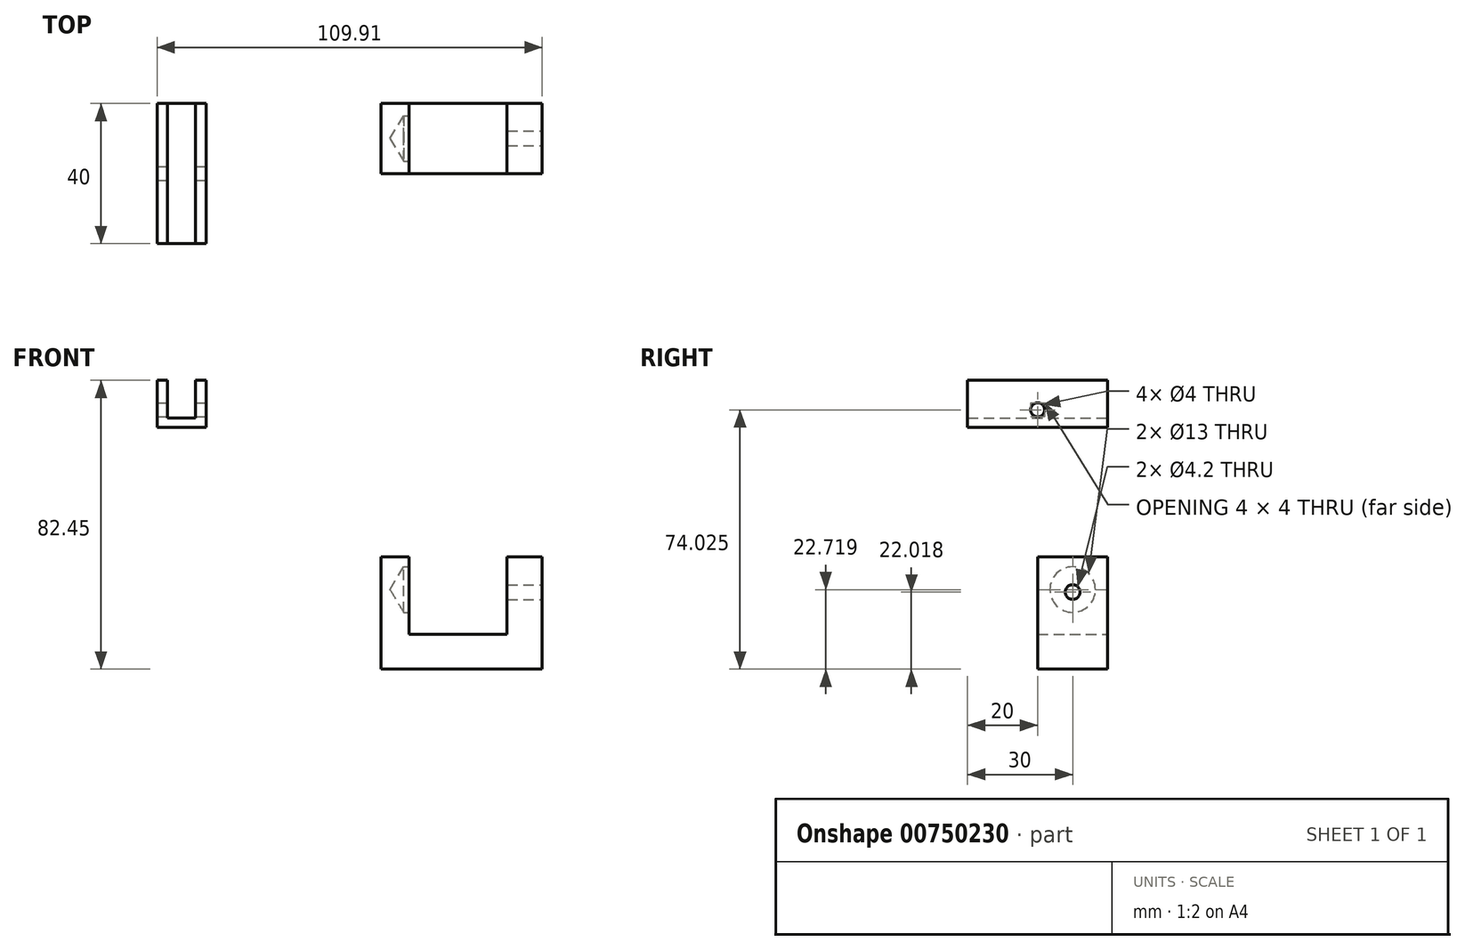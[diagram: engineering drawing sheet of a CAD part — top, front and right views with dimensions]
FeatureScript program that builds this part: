
annotation { "Feature Type Name" : "Feature", "Feature Type Description" : "" }
export const myFeature = defineFeature(function(context is Context, id is Id, definition is map)
    precondition{}
    {
        {
            var Q0;
            Q0=qCreatedBy(makeId("Front.planeOp"),FACE);
            var sketch = newSketch(context, id + "F0", { "sketchPlane" : qUnion([Q0])});
            skLineSegment(sketch, "E0", {"start": v(0, 0) * mm, "end": v(0, -32) * mm});
            skLineSegment(sketch, "E1", {"start": v(0, -32) * mm, "end": v(46, -32) * mm});
            skLineSegment(sketch, "E2", {"start": v(46, -32) * mm, "end": v(46, 0) * mm});
            skLineSegment(sketch, "E3", {"start": v(46, 0) * mm, "end": v(36, 0) * mm});
            skLineSegment(sketch, "E4", {"start": v(36, 0) * mm, "end": v(36, -22) * mm});
            skLineSegment(sketch, "E5", {"start": v(36, -22) * mm, "end": v(8, -22) * mm});
            skLineSegment(sketch, "E6", {"start": v(8, -22) * mm, "end": v(8, 0) * mm});
            skLineSegment(sketch, "E7", {"start": v(8, 0) * mm, "end": v(0, 0) * mm});
            skSolve(sketch);
        }
        {
            var Q0;
            Q0=makeQuery(id+"F0.imprint","IMPRINT",FACE,{"disambiguationData":[TD([[makeQuery(id+"F0.imprint","IMPRINT",EDGE,{"derivedFrom":sQuery(id+"F0.wireOp",EDGE,"E0")}),1.0]])]});
            extrude(context, id + "F1", {"entities" : qUnion([Q0]), "depth" : 20 * mm, "offsetDistance" : 25 * mm});
        }
        {
            var Q0;
            Q0=makeQuery(id+"F1.opExtrude","SWEPT_FACE",FACE,{"disambiguationData":[OSD([sQuery(id+"F0.wireOp",EDGE,"E6")])]});
            var sketch = newSketch(context, id + "F2", { "sketchPlane" : qUnion([Q0])});
            skPoint(sketch, "E8", {"position": v(-10, -9.28) * mm});
            skPoint(sketch, "E8.positionSnap0", {"position": v(-10, 0) * mm});
            skSolve(sketch);
        }
        {
            var Q0;
            Q0=sQuery(id+"F2.wireOp",VERTEX,"E8");
            var Q1;
            Q1=makeQuery(id+"F1.opExtrude","SWEPT_BODY",BODY,{"disambiguationData":[OSD([sQuery(id+"F0.wireOp",EDGE,"E0"),sQuery(id+"F0.wireOp",EDGE,"E1"),sQuery(id+"F0.wireOp",EDGE,"E2"),sQuery(id+"F0.wireOp",EDGE,"E3"),sQuery(id+"F0.wireOp",EDGE,"E4"),sQuery(id+"F0.wireOp",EDGE,"E5"),sQuery(id+"F0.wireOp",EDGE,"E6"),sQuery(id+"F0.wireOp",EDGE,"E7")])]});
            hole(context, id + "F3", {"style" : HoleStyle.SIMPLE, "endStyle" : HoleEndStyle.BLIND, "holeDiameter" : 13 * mm, "majorDiameter" : 5 * mm, "holeDepth" : 1.5 * mm, "isTappedThrough" : true, "tappedDepth" : 12 * mm, "tapClearance" : 3, "startFromSketch" : true, "locations" : qUnion([Q0]), "scope" : qUnion([Q1])});
        }
        {
            var Q0;
            Q0=makeQuery(id+"F1.opExtrude","SWEPT_FACE",FACE,{"disambiguationData":[OSD([sQuery(id+"F0.wireOp",EDGE,"E2")])]});
            var sketch = newSketch(context, id + "F4", { "sketchPlane" : qUnion([Q0])});
            skPoint(sketch, "E9", {"position": v(-10, -9.98) * mm});
            skPoint(sketch, "E9.positionSnap0", {"position": v(-10, 0) * mm});
            skSolve(sketch);
        }
        {
            var Q0;
            Q0=sQuery(id+"F4.wireOp",VERTEX,"E9");
            var Q1;
            Q1=makeQuery(id+"F1.opExtrude","SWEPT_BODY",BODY,{"disambiguationData":[OSD([sQuery(id+"F0.wireOp",EDGE,"E0"),sQuery(id+"F0.wireOp",EDGE,"E1"),sQuery(id+"F0.wireOp",EDGE,"E2"),sQuery(id+"F0.wireOp",EDGE,"E3"),sQuery(id+"F0.wireOp",EDGE,"E4"),sQuery(id+"F0.wireOp",EDGE,"E5"),sQuery(id+"F0.wireOp",EDGE,"E6"),sQuery(id+"F0.wireOp",EDGE,"E7")])]});
            hole(context, id + "F5", {"style" : HoleStyle.SIMPLE, "endStyle" : HoleEndStyle.BLIND, "holeDiameter" : 4.2 * mm, "majorDiameter" : 5 * mm, "holeDepth" : 10 * mm, "isTappedThrough" : true, "tappedDepth" : 12 * mm, "tapClearance" : 3, "startFromSketch" : true, "locations" : qUnion([Q0]), "scope" : qUnion([Q1])});
        }
        {
            var Q0;
            Q0=qCreatedBy(makeId("Front.planeOp"),FACE);
            var sketch = newSketch(context, id + "F6", { "sketchPlane" : qUnion([Q0])});
            skLineSegment(sketch, "E10", {"start": v(-63.91, 50.45) * mm, "end": v(-63.91, 36.99) * mm});
            skLineSegment(sketch, "E11", {"start": v(-63.91, 36.99) * mm, "end": v(-49.91, 36.99) * mm});
            skLineSegment(sketch, "E12", {"start": v(-49.91, 36.99) * mm, "end": v(-49.91, 50.45) * mm});
            skLineSegment(sketch, "E13", {"start": v(-63.91, 50.45) * mm, "end": v(-60.91, 50.45) * mm});
            skLineSegment(sketch, "E14", {"start": v(-60.91, 50.45) * mm, "end": v(-60.91, 39.64) * mm});
            skLineSegment(sketch, "E15", {"start": v(-60.91, 39.64) * mm, "end": v(-52.91, 39.64) * mm});
            skLineSegment(sketch, "E16", {"start": v(-52.91, 39.64) * mm, "end": v(-52.91, 50.45) * mm});
            skLineSegment(sketch, "E17", {"start": v(-52.91, 50.45) * mm, "end": v(-49.91, 50.45) * mm});
            skSolve(sketch);
        }
        {
            var Q0;
            Q0=makeQuery(id+"F6.imprint","IMPRINT",FACE,{"disambiguationData":[TD([[makeQuery(id+"F6.imprint","IMPRINT",EDGE,{"derivedFrom":sQuery(id+"F6.wireOp",EDGE,"E10")}),1.0]])]});
            extrude(context, id + "F7", {"entities" : qUnion([Q0]), "depth" : 40 * mm, "offsetDistance" : 25 * mm});
        }
        {
            var Q0;
            Q0=makeQuery(id+"F7.opExtrude","SWEPT_FACE",FACE,{"disambiguationData":[OSD([sQuery(id+"F6.wireOp",EDGE,"E12")])]});
            var sketch = newSketch(context, id + "F8", { "sketchPlane" : qUnion([Q0])});
            skPoint(sketch, "E18", {"position": v(-20, 42.03) * mm});
            skPoint(sketch, "E18.positionSnap0", {"position": v(-20, 50.45) * mm});
            skSolve(sketch);
        }
        {
            var Q0;
            Q0=sQuery(id+"F8.wireOp",VERTEX,"E18");
            var Q1;
            Q1=makeQuery(id+"F7.opExtrude","SWEPT_BODY",BODY,{"disambiguationData":[OSD([sQuery(id+"F6.wireOp",EDGE,"E10"),sQuery(id+"F6.wireOp",EDGE,"E11"),sQuery(id+"F6.wireOp",EDGE,"E12"),sQuery(id+"F6.wireOp",EDGE,"E13"),sQuery(id+"F6.wireOp",EDGE,"E14"),sQuery(id+"F6.wireOp",EDGE,"E15"),sQuery(id+"F6.wireOp",EDGE,"E16"),sQuery(id+"F6.wireOp",EDGE,"E17")])]});
            hole(context, id + "F9", {"style" : HoleStyle.SIMPLE, "endStyle" : HoleEndStyle.THROUGH, "holeDiameter" : 4 * mm, "majorDiameter" : 5 * mm, "isTappedThrough" : true, "tappedDepth" : 12 * mm, "tapClearance" : 3, "startFromSketch" : true, "locations" : qUnion([Q0]), "scope" : qUnion([Q1])});
        }
    });
